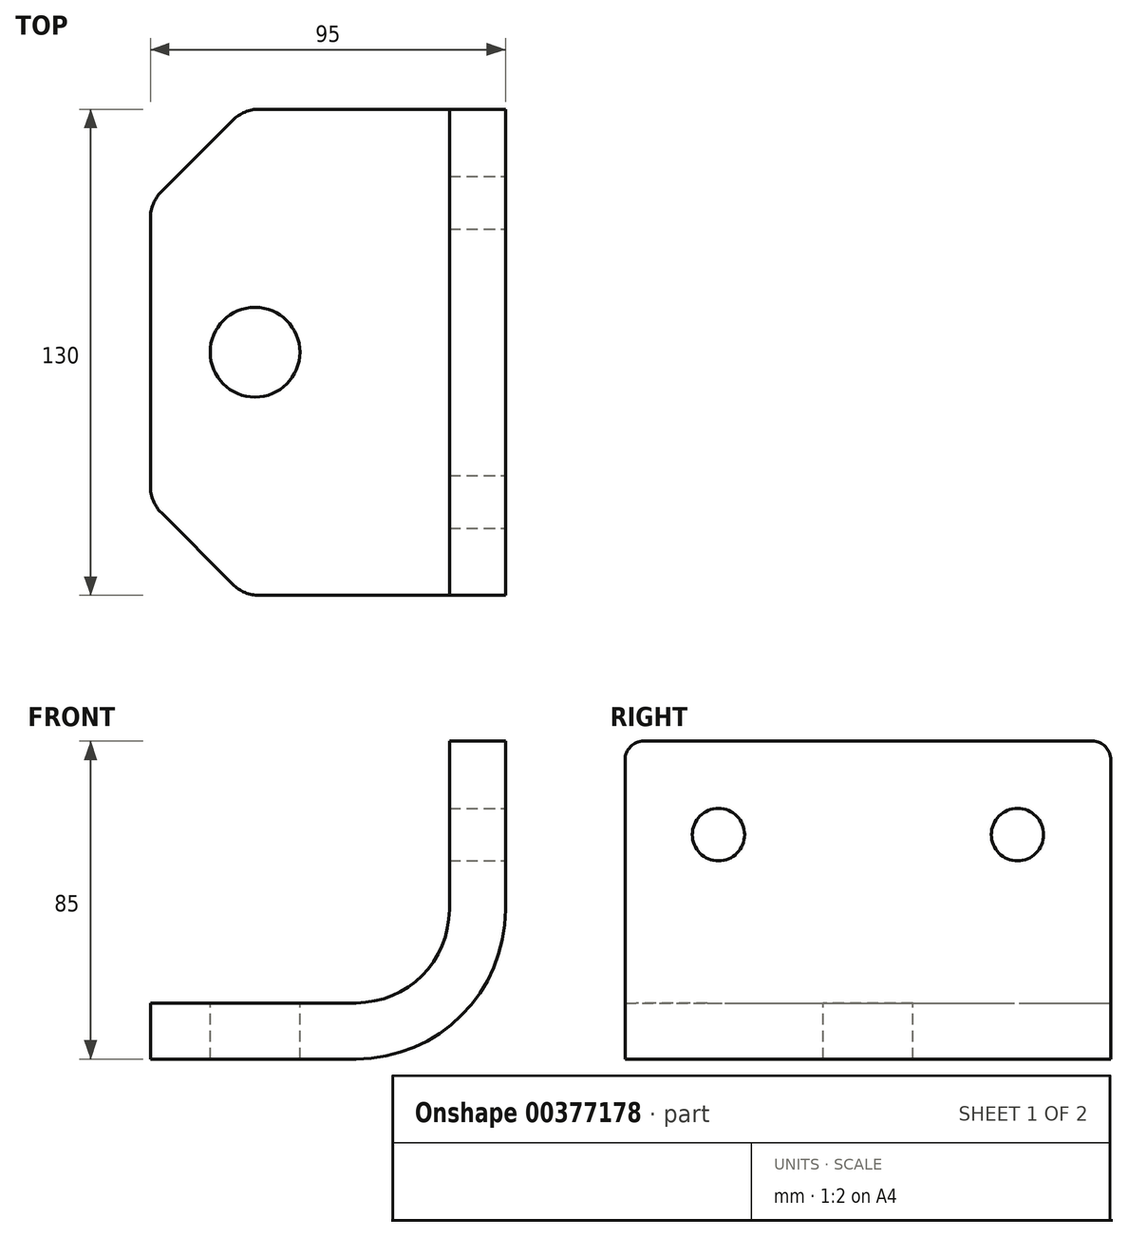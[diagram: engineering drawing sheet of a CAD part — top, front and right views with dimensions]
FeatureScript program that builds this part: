
annotation { "Feature Type Name" : "Feature", "Feature Type Description" : "" }
export const myFeature = defineFeature(function(context is Context, id is Id, definition is map)
    precondition{}
    {
        {
            var Q0;
            Q0=qCreatedBy(makeId("Front.planeOp"),FACE);
            var sketch = newSketch(context, id + "F0", { "sketchPlane" : qUnion([Q0])});
            skLineSegment(sketch, "E0", {"start": v(0, 70) * mm, "end": v(0, 25) * mm});
            skLineSegment(sketch, "E1", {"start": v(-25, 0) * mm, "end": v(-80, 0) * mm});
            skPoint(sketch, "E2.visualSharp", {"position": v(0, 0) * mm});
            skArc(sketch, "E2.filletArc", {"start": v(-25, 0) * mm, "mid": v(-7.32, 7.32) * mm, "end": v(0, 25) * mm});
            skLineSegment(sketch, "E3.0", {"start": v(-25, -15) * mm, "end": v(-80, -15) * mm});
            skArc(sketch, "E3.1", {"start": v(-25, -15) * mm, "mid": v(3.28, -3.28) * mm, "end": v(15, 25) * mm});
            skLineSegment(sketch, "E3.2", {"start": v(15, 70) * mm, "end": v(15, 25) * mm});
            skLineSegment(sketch, "E4", {"start": v(0, 70) * mm, "end": v(15, 70) * mm});
            skLineSegment(sketch, "E5", {"start": v(-80, 0) * mm, "end": v(-80, -15) * mm});
            skSolve(sketch);
        }
        {
            var Q0;
            Q0=qSketchRegion(id+"F0",true);
            extrude(context, id + "F1", {"entities" : qUnion([Q0]), "depth" : 130 * mm});
        }
        {
            var Q0;
            Q0=makeQuery(id+"F1.opExtrude","CAP_EDGE",EDGE,{"disambiguationData":[OSD([sQuery(id+"F0.wireOp",EDGE,"E5")])],"isStart":false});
            var Q1;
            Q1=makeQuery(id+"F1.opExtrude","CAP_EDGE",EDGE,{"disambiguationData":[OSD([sQuery(id+"F0.wireOp",EDGE,"E5")])],"isStart":true});
            chamfer(context, id + "F2", {"entities" : qUnion([Q0, Q1]), "width" : 25 * mm, "tangentPropagation" : true});
        }
        {
            var Q0;
            Q0=makeQuery(id+"F1.opExtrude","SWEPT_FACE",FACE,{"disambiguationData":[OSD([sQuery(id+"F0.wireOp",EDGE,"E1")])]});
            var sketch = newSketch(context, id + "F3", { "sketchPlane" : qUnion([Q0])});
            skPoint(sketch, "E6", {"position": v(-52, -65) * mm});
            skPoint(sketch, "E6.positionSnap0", {"position": v(-80, -65) * mm});
            skSolve(sketch);
        }
        {
            var Q0;
            Q0=sQuery(id+"F3.wireOp",VERTEX,"E6");
            var Q1;
            Q1=makeQuery(id+"F1.opExtrude","SWEPT_BODY",BODY,{"disambiguationData":[OSD([sQuery(id+"F0.wireOp",EDGE,"E0"),sQuery(id+"F0.wireOp",EDGE,"E1"),sQuery(id+"F0.wireOp",EDGE,"E2.filletArc"),sQuery(id+"F0.wireOp",EDGE,"E3.0"),sQuery(id+"F0.wireOp",EDGE,"E3.1"),sQuery(id+"F0.wireOp",EDGE,"E3.2"),sQuery(id+"F0.wireOp",EDGE,"E4"),sQuery(id+"F0.wireOp",EDGE,"E5")])]});
            hole(context, id + "F4", {"style" : HoleStyle.SIMPLE, "endStyle" : HoleEndStyle.THROUGH, "holeDiameter" : 24 * mm, "isTappedThrough" : true, "tappedDepth" : 12 * mm, "tapClearance" : 3, "locations" : qUnion([Q0]), "scope" : qUnion([Q1])});
        }
        {
            var Q0;
            Q0=makeQuery(id+"F1.opExtrude","SWEPT_FACE",FACE,{"disambiguationData":[OSD([sQuery(id+"F0.wireOp",EDGE,"E3.2")])]});
            var sketch = newSketch(context, id + "F5", { "sketchPlane" : qUnion([Q0])});
            skPoint(sketch, "E7", {"position": v(-105, 45) * mm});
            skPoint(sketch, "E8", {"position": v(-25, 45) * mm});
            skSolve(sketch);
        }
        {
            var Q0;
            Q0=sQuery(id+"F5.wireOp",VERTEX,"E7");
            var Q1;
            Q1=sQuery(id+"F5.wireOp",VERTEX,"E8");
            var Q2;
            Q2=makeQuery(id+"F1.opExtrude","SWEPT_BODY",BODY,{"disambiguationData":[OSD([sQuery(id+"F0.wireOp",EDGE,"E0"),sQuery(id+"F0.wireOp",EDGE,"E1"),sQuery(id+"F0.wireOp",EDGE,"E2.filletArc"),sQuery(id+"F0.wireOp",EDGE,"E3.0"),sQuery(id+"F0.wireOp",EDGE,"E3.1"),sQuery(id+"F0.wireOp",EDGE,"E3.2"),sQuery(id+"F0.wireOp",EDGE,"E4"),sQuery(id+"F0.wireOp",EDGE,"E5")])]});
            hole(context, id + "F6", {"style" : HoleStyle.SIMPLE, "endStyle" : HoleEndStyle.THROUGH, "standardTappedOrClearance" : lookupTablePath({ "standard" : "ISO", "size" : "14", "type" : "Drilled" }), "standardBlindInLast" : lookupTablePath({ "standard" : "ISO", "size" : "14", "type" : "Drilled" }), "holeDiameter" : 14 * mm, "isTappedThrough" : true, "tappedDepth" : 12 * mm, "tapClearance" : 3, "locations" : qUnion([Q0, Q1]), "scope" : qUnion([Q2])});
        }
        {
            var Q0;
            {var subQ0=sQuery(id+"F0.wireOp",EDGE,"E5");Q0=makeQuery(id+"F2.opChamfer","BLEND_EDGE",EDGE,{"blendedFrom":[makeQuery(id+"F1.opExtrude","CAP_EDGE",EDGE,{"disambiguationData":[OSD([subQ0])],"isStart":true}),makeQuery(id+"F1.opExtrude","CAP_FACE",FACE,{"disambiguationData":[OSD([sQuery(id+"F0.wireOp",EDGE,"E0"),sQuery(id+"F0.wireOp",EDGE,"E1"),sQuery(id+"F0.wireOp",EDGE,"E2.filletArc"),sQuery(id+"F0.wireOp",EDGE,"E3.0"),sQuery(id+"F0.wireOp",EDGE,"E3.1"),sQuery(id+"F0.wireOp",EDGE,"E3.2"),sQuery(id+"F0.wireOp",EDGE,"E4"),subQ0])],"isStart":true})],"blendedInto":[makeQuery(id+"F1.opExtrude","CAP_FACE",FACE,{"disambiguationData":[OSD([sQuery(id+"F0.wireOp",EDGE,"E0"),sQuery(id+"F0.wireOp",EDGE,"E1"),sQuery(id+"F0.wireOp",EDGE,"E2.filletArc"),sQuery(id+"F0.wireOp",EDGE,"E3.0"),sQuery(id+"F0.wireOp",EDGE,"E3.1"),sQuery(id+"F0.wireOp",EDGE,"E3.2"),sQuery(id+"F0.wireOp",EDGE,"E4"),subQ0])],"isStart":true})]});}
            var Q1;
            {var subQ0=sQuery(id+"F0.wireOp",EDGE,"E5");Q1=makeQuery(id+"F2.opChamfer","BLEND_EDGE",EDGE,{"blendedFrom":[makeQuery(id+"F1.opExtrude","CAP_EDGE",EDGE,{"disambiguationData":[OSD([subQ0])],"isStart":true}),makeQuery(id+"F1.opExtrude","SWEPT_FACE",FACE,{"disambiguationData":[OSD([subQ0])]})],"blendedInto":[makeQuery(id+"F1.opExtrude","SWEPT_FACE",FACE,{"disambiguationData":[OSD([subQ0])]})]});}
            var Q2;
            {var subQ0=sQuery(id+"F0.wireOp",EDGE,"E5");Q2=makeQuery(id+"F2.opChamfer","BLEND_EDGE",EDGE,{"blendedFrom":[makeQuery(id+"F1.opExtrude","CAP_EDGE",EDGE,{"disambiguationData":[OSD([subQ0])],"isStart":false}),makeQuery(id+"F1.opExtrude","SWEPT_FACE",FACE,{"disambiguationData":[OSD([subQ0])]})],"blendedInto":[makeQuery(id+"F1.opExtrude","SWEPT_FACE",FACE,{"disambiguationData":[OSD([subQ0])]})]});}
            var Q3;
            {var subQ0=sQuery(id+"F0.wireOp",EDGE,"E5");Q3=makeQuery(id+"F2.opChamfer","BLEND_EDGE",EDGE,{"blendedFrom":[makeQuery(id+"F1.opExtrude","CAP_EDGE",EDGE,{"disambiguationData":[OSD([subQ0])],"isStart":false}),makeQuery(id+"F1.opExtrude","CAP_FACE",FACE,{"disambiguationData":[OSD([sQuery(id+"F0.wireOp",EDGE,"E0"),sQuery(id+"F0.wireOp",EDGE,"E1"),sQuery(id+"F0.wireOp",EDGE,"E2.filletArc"),sQuery(id+"F0.wireOp",EDGE,"E3.0"),sQuery(id+"F0.wireOp",EDGE,"E3.1"),sQuery(id+"F0.wireOp",EDGE,"E3.2"),sQuery(id+"F0.wireOp",EDGE,"E4"),subQ0])],"isStart":false})],"blendedInto":[makeQuery(id+"F1.opExtrude","CAP_FACE",FACE,{"disambiguationData":[OSD([sQuery(id+"F0.wireOp",EDGE,"E0"),sQuery(id+"F0.wireOp",EDGE,"E1"),sQuery(id+"F0.wireOp",EDGE,"E2.filletArc"),sQuery(id+"F0.wireOp",EDGE,"E3.0"),sQuery(id+"F0.wireOp",EDGE,"E3.1"),sQuery(id+"F0.wireOp",EDGE,"E3.2"),sQuery(id+"F0.wireOp",EDGE,"E4"),subQ0])],"isStart":false})]});}
            fillet(context, id + "F7", {"entities" : qUnion([Q0, Q1, Q2, Q3]), "radius" : 10 * mm, "tangentPropagation" : true, "allowEdgeOverflow" : false});
        }
        {
            var Q0;
            Q0=makeQuery(id+"F1.opExtrude","CAP_EDGE",EDGE,{"disambiguationData":[OSD([sQuery(id+"F0.wireOp",EDGE,"E4")])],"isStart":false});
            var Q1;
            Q1=makeQuery(id+"F1.opExtrude","CAP_EDGE",EDGE,{"disambiguationData":[OSD([sQuery(id+"F0.wireOp",EDGE,"E4")])],"isStart":true});
            fillet(context, id + "F8", {"entities" : qUnion([Q0, Q1]), "radius" : 5 * mm, "tangentPropagation" : true, "allowEdgeOverflow" : false});
        }
    });
